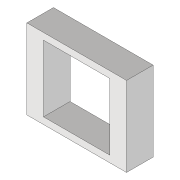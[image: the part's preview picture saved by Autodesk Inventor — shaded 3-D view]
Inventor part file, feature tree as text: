
AUTODESK INVENTOR PART (.ipt)
format: ipt  version: 2020 (Build 240168000, 168)  size: 99,840 bytes
history: native  units: mm
features: extrude x2, sketch x2
ambient origin geometry x8: Origin, YZ Plane, XZ Plane, XY Plane, X Axis, Y Axis, Z Axis, Center Point
bodies: Volumenkörper1 (feature_tree)
feature tree (4):
  extrude  "Extrusion1"  Depth=100.0mm
  extrude  "Extrusion2"  Depth=120.0mm
  sketch  "Skizze1"  dims[d0=100.0mm d1=100.0mm]
  sketch  "Skizze2"  dims[d2=150.0mm d3=120.0mm d4=40.0mm d5=0.0mm d6=10.0mm d7=10.0mm d8=10.0mm d9=10.0mm d10=40.0mm d11=20.0mm d12=20.0mm d13=0.0mm d14=0.0mm]
